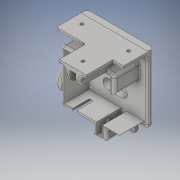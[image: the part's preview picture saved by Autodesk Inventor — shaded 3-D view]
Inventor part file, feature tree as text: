
AUTODESK INVENTOR PART (.ipt)
format: ipt  version: 2016 (Build 200138000, 138)  size: 1,056,768 bytes
history: native  units: in
note: dims shown in document units (in); Inventor stores cm internally (conversion verified against a paired STEP export)
features: sketch x18, plane x4, other x3
ambient origin geometry x8: Origin, YZ Plane, XZ Plane, XY Plane, X Axis, Y Axis, Z Axis, Center Point
bodies: Solid1 (feature_tree)
feature tree (25):
  other  "ankle_holder.ipt"
  other  "Solid1::ankle_holder.ipt"
  other  "TaggingFeature1"
  sketch  "Sketch1"  dims[d0=0.3937in]
  sketch  "Sketch12"
  sketch  "Sketch14"
  sketch  "Sketch17"
  sketch  "Sketch18"
  sketch  "Sketch22"
  sketch  "Sketch24"
  sketch  "Sketch30"
  sketch  "Sketch32"
  sketch  "Sketch33"
  sketch  "Sketch35"
  sketch  "Sketch36"
  sketch  "Sketch37"
  sketch  "Sketch38"
  sketch  "Sketch40"
  sketch  "Sketch41"
  sketch  "Sketch42"
  sketch  "Sketch43"
  plane  "Work Plane1"
  plane  "Work Plane4"
  plane  "Work Plane5"
  plane  "Work Plane6"
